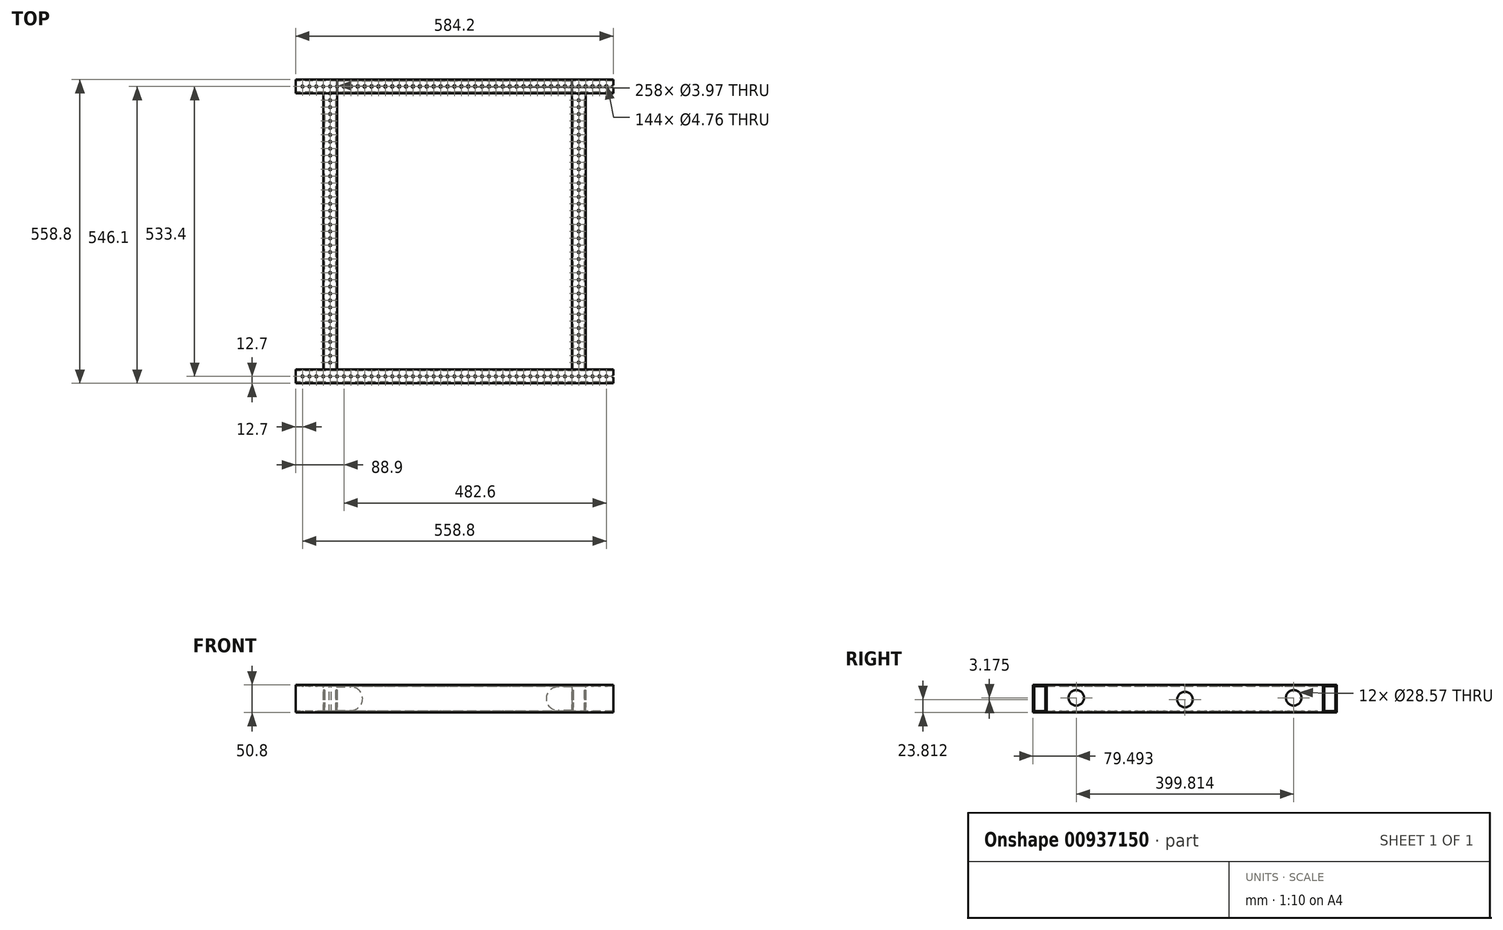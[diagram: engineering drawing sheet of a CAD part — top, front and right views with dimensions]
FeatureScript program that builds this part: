
annotation { "Feature Type Name" : "Feature", "Feature Type Description" : "" }
export const myFeature = defineFeature(function(context is Context, id is Id, definition is map)
    precondition{}
    {
        {
            var Q0;
            Q0=qCreatedBy(makeId("Right.planeOp"),FACE);
            var sketch = newSketch(context, id + "F0", { "sketchPlane" : qUnion([Q0])});
            skLineSegment(sketch, "E0.bottom", {"start": v(12.7, -25.4) * mm, "end": v(-12.7, -25.4) * mm});
            skLineSegment(sketch, "E0.top", {"start": v(12.7, 25.4) * mm, "end": v(-12.7, 25.4) * mm});
            skLineSegment(sketch, "E0.left", {"start": v(12.7, -25.4) * mm, "end": v(12.7, 25.4) * mm});
            skLineSegment(sketch, "E0.right", {"start": v(-12.7, -25.4) * mm, "end": v(-12.7, 25.4) * mm});
            skPoint(sketch, "E0.middle", {"position": v(0, 0) * mm});
            skLineSegment(sketch, "E1.0", {"start": v(10.16, 22.86) * mm, "end": v(-10.16, 22.86) * mm});
            skLineSegment(sketch, "E1.1", {"start": v(10.16, -22.86) * mm, "end": v(10.16, 22.86) * mm});
            skLineSegment(sketch, "E1.2", {"start": v(10.16, -22.86) * mm, "end": v(-10.16, -22.86) * mm});
            skLineSegment(sketch, "E1.3", {"start": v(-10.16, -22.86) * mm, "end": v(-10.16, 22.86) * mm});
            skSolve(sketch);
        }
        {
            var Q0;
            Q0 = qSketchRegion(id + "F0", true);
            extrude(context, id + "F1", {"entities" : qUnion([Q0]), "endBound" : BoundingType.SYMMETRIC, "depth" : 584.2 * mm, "offsetDistance" : 25.4 * mm});
        }
        {
            var Q0;
            Q0=makeQuery(id+"F1.opExtrude","SWEPT_FACE",FACE,{"disambiguationData":[OSD([sQuery(id+"F0.wireOp",EDGE,"E0.top")])]});
            var sketch = newSketch(context, id + "F2", { "sketchPlane" : qUnion([Q0])});
            skLineSegment(sketch, "E2", {"start": v(-292.1, 0) * mm, "end": v(292.1, 0) * mm, "construction": true});
            skCircle(sketch, "E3", {"center": v(-279.4, 0) * mm, "radius": 1.98 * mm});
            skCircle(sketch, "E4.1.0.0", {"center": v(-266.7, 0) * mm, "radius": 1.98 * mm});
            skCircle(sketch, "E4.2.0.0", {"center": v(-254, 0) * mm, "radius": 1.98 * mm});
            skCircle(sketch, "E4.3.0.0", {"center": v(-241.3, 0) * mm, "radius": 1.98 * mm});
            skCircle(sketch, "E4.4.0.0", {"center": v(-228.6, 0) * mm, "radius": 1.98 * mm});
            skCircle(sketch, "E4.5.0.0", {"center": v(-215.9, 0) * mm, "radius": 1.98 * mm});
            skCircle(sketch, "E4.6.0.0", {"center": v(-203.2, 0) * mm, "radius": 1.98 * mm});
            skCircle(sketch, "E4.7.0.0", {"center": v(-190.5, 0) * mm, "radius": 1.98 * mm});
            skCircle(sketch, "E4.8.0.0", {"center": v(-177.8, 0) * mm, "radius": 1.98 * mm});
            skCircle(sketch, "E4.9.0.0", {"center": v(-165.1, 0) * mm, "radius": 1.98 * mm});
            skCircle(sketch, "E4.10.0.0", {"center": v(-152.4, 0) * mm, "radius": 1.98 * mm});
            skCircle(sketch, "E4.11.0.0", {"center": v(-139.7, 0) * mm, "radius": 1.98 * mm});
            skCircle(sketch, "E4.12.0.0", {"center": v(-127, 0) * mm, "radius": 1.98 * mm});
            skCircle(sketch, "E4.13.0.0", {"center": v(-114.3, 0) * mm, "radius": 1.98 * mm});
            skCircle(sketch, "E4.14.0.0", {"center": v(-101.6, 0) * mm, "radius": 1.98 * mm});
            skCircle(sketch, "E4.15.0.0", {"center": v(-88.9, 0) * mm, "radius": 1.98 * mm});
            skCircle(sketch, "E4.16.0.0", {"center": v(-76.2, 0) * mm, "radius": 1.98 * mm});
            skCircle(sketch, "E4.17.0.0", {"center": v(-63.5, 0) * mm, "radius": 1.98 * mm});
            skCircle(sketch, "E4.18.0.0", {"center": v(-50.8, 0) * mm, "radius": 1.98 * mm});
            skCircle(sketch, "E4.19.0.0", {"center": v(-38.1, 0) * mm, "radius": 1.98 * mm});
            skCircle(sketch, "E4.20.0.0", {"center": v(-25.4, 0) * mm, "radius": 1.98 * mm});
            skCircle(sketch, "E4.21.0.0", {"center": v(-12.7, 0) * mm, "radius": 1.98 * mm});
            skCircle(sketch, "E4.22.0.0", {"center": v(0, 0) * mm, "radius": 1.98 * mm});
            skCircle(sketch, "E4.23.0.0", {"center": v(12.7, 0) * mm, "radius": 1.98 * mm});
            skCircle(sketch, "E4.24.0.0", {"center": v(25.4, 0) * mm, "radius": 1.98 * mm});
            skCircle(sketch, "E4.25.0.0", {"center": v(38.1, 0) * mm, "radius": 1.98 * mm});
            skCircle(sketch, "E4.26.0.0", {"center": v(50.8, 0) * mm, "radius": 1.98 * mm});
            skCircle(sketch, "E4.27.0.0", {"center": v(63.5, 0) * mm, "radius": 1.98 * mm});
            skCircle(sketch, "E4.28.0.0", {"center": v(76.2, 0) * mm, "radius": 1.98 * mm});
            skCircle(sketch, "E4.29.0.0", {"center": v(88.9, 0) * mm, "radius": 1.98 * mm});
            skCircle(sketch, "E4.30.0.0", {"center": v(101.6, 0) * mm, "radius": 1.98 * mm});
            skCircle(sketch, "E4.31.0.0", {"center": v(114.3, 0) * mm, "radius": 1.98 * mm});
            skCircle(sketch, "E4.32.0.0", {"center": v(127, 0) * mm, "radius": 1.98 * mm});
            skCircle(sketch, "E4.33.0.0", {"center": v(139.7, 0) * mm, "radius": 1.98 * mm});
            skCircle(sketch, "E4.34.0.0", {"center": v(152.4, 0) * mm, "radius": 1.98 * mm});
            skCircle(sketch, "E4.35.0.0", {"center": v(165.1, 0) * mm, "radius": 1.98 * mm});
            skCircle(sketch, "E4.36.0.0", {"center": v(177.8, 0) * mm, "radius": 1.98 * mm});
            skCircle(sketch, "E4.37.0.0", {"center": v(190.5, 0) * mm, "radius": 1.98 * mm});
            skCircle(sketch, "E4.38.0.0", {"center": v(203.2, 0) * mm, "radius": 1.98 * mm});
            skCircle(sketch, "E4.39.0.0", {"center": v(215.9, 0) * mm, "radius": 1.98 * mm});
            skCircle(sketch, "E4.40.0.0", {"center": v(228.6, 0) * mm, "radius": 1.98 * mm});
            skCircle(sketch, "E4.41.0.0", {"center": v(241.3, 0) * mm, "radius": 1.98 * mm});
            skCircle(sketch, "E4.42.0.0", {"center": v(254, 0) * mm, "radius": 1.98 * mm});
            skCircle(sketch, "E4.43.0.0", {"center": v(266.7, 0) * mm, "radius": 1.98 * mm});
            skCircle(sketch, "E4.44.0.0", {"center": v(279.4, 0) * mm, "radius": 1.98 * mm});
            skCircle(sketch, "E4.45.0.0", {"center": v(292.1, 0) * mm, "radius": 1.98 * mm});
            skCircle(sketch, "E4.46.0.0", {"center": v(304.8, 0) * mm, "radius": 1.98 * mm});
            skCircle(sketch, "E4.47.0.0", {"center": v(317.5, 0) * mm, "radius": 1.98 * mm});
            skCircle(sketch, "E4.48.0.0", {"center": v(330.2, 0) * mm, "radius": 1.98 * mm});
            skCircle(sketch, "E4.49.0.0", {"center": v(342.9, 0) * mm, "radius": 1.98 * mm});
            skCircle(sketch, "E4.50.0.0", {"center": v(355.6, 0) * mm, "radius": 1.98 * mm});
            skCircle(sketch, "E4.51.0.0", {"center": v(368.3, 0) * mm, "radius": 1.98 * mm});
            skCircle(sketch, "E4.52.0.0", {"center": v(381, 0) * mm, "radius": 1.98 * mm});
            skCircle(sketch, "E4.53.0.0", {"center": v(393.7, 0) * mm, "radius": 1.98 * mm});
            skCircle(sketch, "E4.54.0.0", {"center": v(406.4, 0) * mm, "radius": 1.98 * mm});
            skCircle(sketch, "E4.55.0.0", {"center": v(419.1, 0) * mm, "radius": 1.98 * mm});
            skCircle(sketch, "E4.56.0.0", {"center": v(431.8, 0) * mm, "radius": 1.98 * mm});
            skCircle(sketch, "E4.57.0.0", {"center": v(444.5, 0) * mm, "radius": 1.98 * mm});
            skCircle(sketch, "E4.58.0.0", {"center": v(457.2, 0) * mm, "radius": 1.98 * mm});
            skCircle(sketch, "E4.59.0.0", {"center": v(469.9, 0) * mm, "radius": 1.98 * mm});
            skLineSegment(sketch, "E4.direction1", {"start": v(-279.4, 0) * mm, "end": v(-266.7, 0) * mm, "construction": true});
            skSolve(sketch);
        }
        {
            var Q0;
            Q0 = qSketchRegion(id + "F2", true);
            extrude(context, id + "F3", {"entities" : qUnion([Q0]), "operationType" : NewBodyOperationType.REMOVE, "oppositeDirection" : true, "depth" : 76.2 * mm, "offsetDistance" : 25.4 * mm});
        }
        {
            var Q0;
            Q0=makeQuery(id+"F1.opExtrude","SWEPT_BODY",BODY,{"disambiguationData":[OSD([sQuery(id+"F0.wireOp",EDGE,"E0.bottom"),sQuery(id+"F0.wireOp",EDGE,"E0.top"),sQuery(id+"F0.wireOp",EDGE,"E0.left"),sQuery(id+"F0.wireOp",EDGE,"E0.right"),sQuery(id+"F0.wireOp",EDGE,"E1.0"),sQuery(id+"F0.wireOp",EDGE,"E1.1"),sQuery(id+"F0.wireOp",EDGE,"E1.2"),sQuery(id+"F0.wireOp",EDGE,"E1.3")])]});
            transform(context, id + "F4", {"entities" : qUnion([Q0]), "transformType" : TransformType.TRANSLATION_3D, "dx" : 0 * mm, "dy" : -533.4 * mm, "dz" : 0 * mm, "makeCopy" : true});
        }
        {
            var Q0;
            Q0=makeQuery(id+"F1.opExtrude","SWEPT_BODY",BODY,{"disambiguationData":[OSD([sQuery(id+"F0.wireOp",EDGE,"E0.bottom"),sQuery(id+"F0.wireOp",EDGE,"E0.top"),sQuery(id+"F0.wireOp",EDGE,"E0.left"),sQuery(id+"F0.wireOp",EDGE,"E0.right"),sQuery(id+"F0.wireOp",EDGE,"E1.0"),sQuery(id+"F0.wireOp",EDGE,"E1.1"),sQuery(id+"F0.wireOp",EDGE,"E1.2"),sQuery(id+"F0.wireOp",EDGE,"E1.3")])]});
            var Q1;
            Q1=makeQuery(id+"F1.opExtrude","CAP_EDGE",EDGE,{"disambiguationData":[OSD([sQuery(id+"F0.wireOp",EDGE,"E0.right")])],"isStart":true});
            transform(context, id + "F5", {"entities" : qUnion([Q0]), "transformType" : TransformType.ROTATION, "transformAxis" : qUnion([Q1]), "angle" : 270 * degree, "makeCopy" : true});
        }
        {
            var Q0;
            Q0=makeQuery(id+"F5.opPattern","COPY",BODY,{"derivedFrom":makeQuery(id+"F1.opExtrude","SWEPT_BODY",BODY,{"disambiguationData":[OSD([sQuery(id+"F0.wireOp",EDGE,"E0.bottom"),sQuery(id+"F0.wireOp",EDGE,"E0.top"),sQuery(id+"F0.wireOp",EDGE,"E0.left"),sQuery(id+"F0.wireOp",EDGE,"E0.right"),sQuery(id+"F0.wireOp",EDGE,"E1.0"),sQuery(id+"F0.wireOp",EDGE,"E1.1"),sQuery(id+"F0.wireOp",EDGE,"E1.2"),sQuery(id+"F0.wireOp",EDGE,"E1.3")])]}),"instanceName":"1"});
            deleteBodies(context, id + "F6", {"entities" : qUnion([Q0])});
        }
        {
            var Q0;
            Q0=makeQuery(id+"F1.opExtrude","SWEPT_FACE",FACE,{"disambiguationData":[OSD([sQuery(id+"F0.wireOp",EDGE,"E0.right")])]});
            var sketch = newSketch(context, id + "F7", { "sketchPlane" : qUnion([Q0])});
            skLineSegment(sketch, "E5.bottom", {"start": v(-215.9, -25.4) * mm, "end": v(-241.3, -25.4) * mm});
            skLineSegment(sketch, "E5.top", {"start": v(-215.9, 25.4) * mm, "end": v(-241.3, 25.4) * mm});
            skLineSegment(sketch, "E5.left", {"start": v(-215.9, -25.4) * mm, "end": v(-215.9, 25.4) * mm});
            skLineSegment(sketch, "E5.right", {"start": v(-241.3, -25.4) * mm, "end": v(-241.3, 25.4) * mm});
            skPoint(sketch, "E5.middle", {"position": v(-228.6, 0) * mm});
            skLineSegment(sketch, "E6.0", {"start": v(-218.44, 22.86) * mm, "end": v(-238.76, 22.86) * mm});
            skLineSegment(sketch, "E6.1", {"start": v(-218.44, -22.86) * mm, "end": v(-218.44, 22.86) * mm});
            skLineSegment(sketch, "E6.2", {"start": v(-218.44, -22.86) * mm, "end": v(-238.76, -22.86) * mm});
            skLineSegment(sketch, "E6.3", {"start": v(-238.76, -22.86) * mm, "end": v(-238.76, 22.86) * mm});
            skSolve(sketch);
        }
        {
            var Q0;
            Q0 = qSketchRegion(id + "F7", true);
            extrude(context, id + "F8", {"entities" : qUnion([Q0]), "depth" : 508 * mm, "offsetDistance" : 25.4 * mm});
        }
        {
            var Q0;
            Q0=makeQuery(id+"F8.opExtrude","SWEPT_FACE",FACE,{"disambiguationData":[OSD([sQuery(id+"F7.wireOp",EDGE,"E5.top")])]});
            var sketch = newSketch(context, id + "F9", { "sketchPlane" : qUnion([Q0])});
            skLineSegment(sketch, "E7", {"start": v(-228.6, -12.7) * mm, "end": v(-228.6, -520.7) * mm, "construction": true});
            skCircle(sketch, "E8", {"center": v(-228.6, -12.7) * mm, "radius": 1.98 * mm});
            skCircle(sketch, "E9.0.1.0", {"center": v(-228.6, -25.4) * mm, "radius": 1.98 * mm});
            skCircle(sketch, "E9.0.2.0", {"center": v(-228.6, -38.1) * mm, "radius": 1.98 * mm});
            skCircle(sketch, "E9.0.3.0", {"center": v(-228.6, -50.8) * mm, "radius": 1.98 * mm});
            skCircle(sketch, "E9.0.4.0", {"center": v(-228.6, -63.5) * mm, "radius": 1.98 * mm});
            skCircle(sketch, "E9.0.5.0", {"center": v(-228.6, -76.2) * mm, "radius": 1.98 * mm});
            skCircle(sketch, "E9.0.6.0", {"center": v(-228.6, -88.9) * mm, "radius": 1.98 * mm});
            skCircle(sketch, "E9.0.7.0", {"center": v(-228.6, -101.6) * mm, "radius": 1.98 * mm});
            skCircle(sketch, "E9.0.8.0", {"center": v(-228.6, -114.3) * mm, "radius": 1.98 * mm});
            skCircle(sketch, "E9.0.9.0", {"center": v(-228.6, -127) * mm, "radius": 1.98 * mm});
            skCircle(sketch, "E9.0.10.0", {"center": v(-228.6, -139.7) * mm, "radius": 1.98 * mm});
            skCircle(sketch, "E9.0.11.0", {"center": v(-228.6, -152.4) * mm, "radius": 1.98 * mm});
            skCircle(sketch, "E9.0.12.0", {"center": v(-228.6, -165.1) * mm, "radius": 1.98 * mm});
            skCircle(sketch, "E9.0.13.0", {"center": v(-228.6, -177.8) * mm, "radius": 1.98 * mm});
            skCircle(sketch, "E9.0.14.0", {"center": v(-228.6, -190.5) * mm, "radius": 1.98 * mm});
            skCircle(sketch, "E9.0.15.0", {"center": v(-228.6, -203.2) * mm, "radius": 1.98 * mm});
            skCircle(sketch, "E9.0.16.0", {"center": v(-228.6, -215.9) * mm, "radius": 1.98 * mm});
            skCircle(sketch, "E9.0.17.0", {"center": v(-228.6, -228.6) * mm, "radius": 1.98 * mm});
            skCircle(sketch, "E9.0.18.0", {"center": v(-228.6, -241.3) * mm, "radius": 1.98 * mm});
            skCircle(sketch, "E9.0.19.0", {"center": v(-228.6, -254) * mm, "radius": 1.98 * mm});
            skCircle(sketch, "E9.0.20.0", {"center": v(-228.6, -266.7) * mm, "radius": 1.98 * mm});
            skCircle(sketch, "E9.0.21.0", {"center": v(-228.6, -279.4) * mm, "radius": 1.98 * mm});
            skCircle(sketch, "E9.0.22.0", {"center": v(-228.6, -292.1) * mm, "radius": 1.98 * mm});
            skCircle(sketch, "E9.0.23.0", {"center": v(-228.6, -304.8) * mm, "radius": 1.98 * mm});
            skCircle(sketch, "E9.0.24.0", {"center": v(-228.6, -317.5) * mm, "radius": 1.98 * mm});
            skCircle(sketch, "E9.0.25.0", {"center": v(-228.6, -330.2) * mm, "radius": 1.98 * mm});
            skCircle(sketch, "E9.0.26.0", {"center": v(-228.6, -342.9) * mm, "radius": 1.98 * mm});
            skCircle(sketch, "E9.0.27.0", {"center": v(-228.6, -355.6) * mm, "radius": 1.98 * mm});
            skCircle(sketch, "E9.0.28.0", {"center": v(-228.6, -368.3) * mm, "radius": 1.98 * mm});
            skCircle(sketch, "E9.0.29.0", {"center": v(-228.6, -381) * mm, "radius": 1.98 * mm});
            skCircle(sketch, "E9.0.30.0", {"center": v(-228.6, -393.7) * mm, "radius": 1.98 * mm});
            skCircle(sketch, "E9.0.31.0", {"center": v(-228.6, -406.4) * mm, "radius": 1.98 * mm});
            skLineSegment(sketch, "E9.direction1", {"start": v(-228.6, -12.7) * mm, "end": v(-190.5, -12.7) * mm, "construction": true});
            skLineSegment(sketch, "E9.direction2", {"start": v(-228.6, -12.7) * mm, "end": v(-228.6, -25.4) * mm, "construction": true});
            skCircle(sketch, "E10.0.0.32", {"center": v(-228.6, -419.1) * mm, "radius": 1.98 * mm});
            skCircle(sketch, "E10.0.0.33", {"center": v(-228.6, -431.8) * mm, "radius": 1.98 * mm});
            skCircle(sketch, "E10.0.0.34", {"center": v(-228.6, -444.5) * mm, "radius": 1.98 * mm});
            skCircle(sketch, "E10.0.0.35", {"center": v(-228.6, -457.2) * mm, "radius": 1.98 * mm});
            skCircle(sketch, "E10.0.0.36", {"center": v(-228.6, -469.9) * mm, "radius": 1.98 * mm});
            skCircle(sketch, "E10.0.0.37", {"center": v(-228.6, -482.6) * mm, "radius": 1.98 * mm});
            skCircle(sketch, "E10.0.0.38", {"center": v(-228.6, -495.3) * mm, "radius": 1.98 * mm});
            skCircle(sketch, "E10.0.0.39", {"center": v(-228.6, -508) * mm, "radius": 1.98 * mm});
            skSolve(sketch);
        }
        {
            var Q0;
            Q0 = qSketchRegion(id + "F9", true);
            extrude(context, id + "F10", {"entities" : qUnion([Q0]), "operationType" : NewBodyOperationType.REMOVE, "oppositeDirection" : true, "depth" : 76.2 * mm, "offsetDistance" : 25.4 * mm});
        }
        {
            var Q0;
            Q0=makeQuery(id+"F8.opExtrude","SWEPT_FACE",FACE,{"disambiguationData":[OSD([sQuery(id+"F7.wireOp",EDGE,"E5.right")])]});
            var sketch = newSketch(context, id + "F11", { "sketchPlane" : qUnion([Q0])});
            skLineSegment(sketch, "E11", {"start": v(12.7, 0) * mm, "end": v(520.7, 0) * mm, "construction": true});
            skLineSegment(sketch, "E12", {"start": v(266.7, -25.4) * mm, "end": v(266.7, 25.4) * mm, "construction": true});
            skCircle(sketch, "E13", {"center": v(266.7, -1.59) * mm, "radius": 14.29 * mm});
            skCircle(sketch, "E14", {"center": v(466.6, 1.59) * mm, "radius": 14.29 * mm});
            skCircle(sketch, "E15.MirrorC", {"center": v(66.8, 1.59) * mm, "radius": 14.29 * mm});
            skSolve(sketch);
        }
        {
            var Q0;
            Q0 = qSketchRegion(id + "F11", true);
            extrude(context, id + "F12", {"entities" : qUnion([Q0]), "operationType" : NewBodyOperationType.REMOVE, "endBound" : BoundingType.SYMMETRIC, "oppositeDirection" : true, "depth" : 1524 * mm, "offsetDistance" : 25.4 * mm});
        }
        {
            var Q0;
            Q0=makeQuery(id+"F8.opExtrude","SWEPT_BODY",BODY,{"disambiguationData":[OSD([sQuery(id+"F7.wireOp",EDGE,"E5.bottom"),sQuery(id+"F7.wireOp",EDGE,"E5.top"),sQuery(id+"F7.wireOp",EDGE,"E5.left"),sQuery(id+"F7.wireOp",EDGE,"E5.right"),sQuery(id+"F7.wireOp",EDGE,"E6.0"),sQuery(id+"F7.wireOp",EDGE,"E6.1"),sQuery(id+"F7.wireOp",EDGE,"E6.2"),sQuery(id+"F7.wireOp",EDGE,"E6.3")])]});
            var Q1;
            Q1=qCreatedBy(makeId("Right.planeOp"),FACE);
            mirror(context, id + "F13", {"entities" : qUnion([Q0]), "mirrorPlane" : qUnion([Q1])});
        }
        {
            var Q0;
            Q0=qCreatedBy(makeId("Right.planeOp"),FACE);
            var sketch = newSketch(context, id + "F14", { "sketchPlane" : qUnion([Q0])});
            skLineSegment(sketch, "E16.0", {"start": v(12.7, -25.4) * mm, "end": v(-12.7, -25.4) * mm});
            skLineSegment(sketch, "E16.1", {"start": v(-12.7, -25.4) * mm, "end": v(-12.7, 25.4) * mm});
            skLineSegment(sketch, "E16.2", {"start": v(10.16, 22.86) * mm, "end": v(-10.16, 22.86) * mm});
            skLineSegment(sketch, "E16.3", {"start": v(10.16, -22.86) * mm, "end": v(10.16, 22.86) * mm});
            skLineSegment(sketch, "E16.4", {"start": v(10.16, -22.86) * mm, "end": v(-10.16, -22.86) * mm});
            skLineSegment(sketch, "E16.5", {"start": v(-10.16, -22.86) * mm, "end": v(-10.16, 22.86) * mm});
            skLineSegment(sketch, "E17.0", {"start": v(12.7, 25.4) * mm, "end": v(-12.7, 25.4) * mm});
            skLineSegment(sketch, "E17.1", {"start": v(12.7, -25.4) * mm, "end": v(12.7, 25.4) * mm});
            skSolve(sketch);
        }
        {
            var Q0;
            Q0 = qSketchRegion(id + "F14", true);
            var Q1;
            Q1=makeQuery(id+"F8.opExtrude","SWEPT_FACE",FACE,{"disambiguationData":[OSD([sQuery(id+"F7.wireOp",EDGE,"E5.left")])]});
            var Q2;
            Q2=makeQuery(id+"F13.opPattern","COPY",FACE,{"derivedFrom":makeQuery(id+"F8.opExtrude","SWEPT_FACE",FACE,{"disambiguationData":[OSD([sQuery(id+"F7.wireOp",EDGE,"E5.left")])]}),"instanceName":"1"});
            extrude(context, id + "F15", {"entities" : qUnion([Q0]), "endBound" : BoundingType.UP_TO_SURFACE, "oppositeDirection" : true, "depth" : 25.4 * mm, "endBoundEntityFace" : qUnion([Q1]), "offsetDistance" : 25.4 * mm, "hasSecondDirection" : true, "secondDirectionBound" : SecondDirectionBoundingType.UP_TO_SURFACE, "secondDirectionOppositeDirection" : false, "secondDirectionDepth" : 25.4 * mm, "secondDirectionBoundEntityFace" : qUnion([Q2])});
        }
        {
            var Q0;
            Q0=makeQuery(id+"F15.opExtrude","SWEPT_FACE",FACE,{"disambiguationData":[OSD([sQuery(id+"F14.wireOp",EDGE,"E17.0")])]});
            var sketch = newSketch(context, id + "F16", { "sketchPlane" : qUnion([Q0])});
            skCircle(sketch, "E18", {"center": v(-203.2, 0) * mm, "radius": 2.38 * mm});
            skPoint(sketch, "E18.centerSnap0", {"position": v(-215.9, 0) * mm});
            skCircle(sketch, "E19.1.0.0", {"center": v(-190.5, 0) * mm, "radius": 2.38 * mm});
            skCircle(sketch, "E19.2.0.0", {"center": v(-177.8, 0) * mm, "radius": 2.38 * mm});
            skCircle(sketch, "E19.3.0.0", {"center": v(-165.1, 0) * mm, "radius": 2.38 * mm});
            skCircle(sketch, "E19.4.0.0", {"center": v(-152.4, 0) * mm, "radius": 2.38 * mm});
            skCircle(sketch, "E19.5.0.0", {"center": v(-139.7, 0) * mm, "radius": 2.38 * mm});
            skCircle(sketch, "E19.6.0.0", {"center": v(-127, 0) * mm, "radius": 2.38 * mm});
            skCircle(sketch, "E19.7.0.0", {"center": v(-114.3, 0) * mm, "radius": 2.38 * mm});
            skCircle(sketch, "E19.8.0.0", {"center": v(-101.6, 0) * mm, "radius": 2.38 * mm});
            skCircle(sketch, "E19.9.0.0", {"center": v(-88.9, 0) * mm, "radius": 2.38 * mm});
            skCircle(sketch, "E19.10.0.0", {"center": v(-76.2, 0) * mm, "radius": 2.38 * mm});
            skCircle(sketch, "E19.11.0.0", {"center": v(-63.5, 0) * mm, "radius": 2.38 * mm});
            skCircle(sketch, "E19.12.0.0", {"center": v(-50.8, 0) * mm, "radius": 2.38 * mm});
            skCircle(sketch, "E19.13.0.0", {"center": v(-38.1, 0) * mm, "radius": 2.38 * mm});
            skCircle(sketch, "E19.14.0.0", {"center": v(-25.4, 0) * mm, "radius": 2.38 * mm});
            skCircle(sketch, "E19.15.0.0", {"center": v(-12.7, 0) * mm, "radius": 2.38 * mm});
            skCircle(sketch, "E19.16.0.0", {"center": v(0, 0) * mm, "radius": 2.38 * mm});
            skCircle(sketch, "E19.17.0.0", {"center": v(12.7, 0) * mm, "radius": 2.38 * mm});
            skCircle(sketch, "E19.18.0.0", {"center": v(25.4, 0) * mm, "radius": 2.38 * mm});
            skCircle(sketch, "E19.19.0.0", {"center": v(38.1, 0) * mm, "radius": 2.38 * mm});
            skCircle(sketch, "E19.20.0.0", {"center": v(50.8, 0) * mm, "radius": 2.38 * mm});
            skCircle(sketch, "E19.21.0.0", {"center": v(63.5, 0) * mm, "radius": 2.38 * mm});
            skCircle(sketch, "E19.22.0.0", {"center": v(76.2, 0) * mm, "radius": 2.38 * mm});
            skCircle(sketch, "E19.23.0.0", {"center": v(88.9, 0) * mm, "radius": 2.38 * mm});
            skCircle(sketch, "E19.24.0.0", {"center": v(101.6, 0) * mm, "radius": 2.38 * mm});
            skCircle(sketch, "E19.25.0.0", {"center": v(114.3, 0) * mm, "radius": 2.38 * mm});
            skCircle(sketch, "E19.26.0.0", {"center": v(127, 0) * mm, "radius": 2.38 * mm});
            skCircle(sketch, "E19.27.0.0", {"center": v(139.7, 0) * mm, "radius": 2.38 * mm});
            skCircle(sketch, "E19.28.0.0", {"center": v(152.4, 0) * mm, "radius": 2.38 * mm});
            skCircle(sketch, "E19.29.0.0", {"center": v(165.1, 0) * mm, "radius": 2.38 * mm});
            skCircle(sketch, "E19.30.0.0", {"center": v(177.8, 0) * mm, "radius": 2.38 * mm});
            skCircle(sketch, "E19.31.0.0", {"center": v(190.5, 0) * mm, "radius": 2.38 * mm});
            skCircle(sketch, "E19.32.0.0", {"center": v(203.2, 0) * mm, "radius": 2.38 * mm});
            skCircle(sketch, "E19.33.0.0", {"center": v(215.9, 0) * mm, "radius": 2.38 * mm});
            skCircle(sketch, "E19.34.0.0", {"center": v(228.6, 0) * mm, "radius": 2.38 * mm});
            skCircle(sketch, "E19.35.0.0", {"center": v(241.3, 0) * mm, "radius": 2.38 * mm});
            skCircle(sketch, "E19.36.0.0", {"center": v(254, 0) * mm, "radius": 2.38 * mm});
            skCircle(sketch, "E19.37.0.0", {"center": v(266.7, 0) * mm, "radius": 2.38 * mm});
            skCircle(sketch, "E19.38.0.0", {"center": v(279.4, 0) * mm, "radius": 2.38 * mm});
            skCircle(sketch, "E19.39.0.0", {"center": v(292.1, 0) * mm, "radius": 2.38 * mm});
            skLineSegment(sketch, "E19.direction1", {"start": v(-203.2, 0) * mm, "end": v(-190.5, 0) * mm, "construction": true});
            skSolve(sketch);
        }
        {
            var Q0;
            Q0 = qSketchRegion(id + "F16", true);
            extrude(context, id + "F17", {"entities" : qUnion([Q0]), "operationType" : NewBodyOperationType.REMOVE, "endBound" : BoundingType.THROUGH_ALL, "oppositeDirection" : true, "depth" : 25.4 * mm, "offsetDistance" : 25.4 * mm});
        }
        {
            var Q0;
            {var subQ0=sQuery(id+"F7.wireOp",EDGE,"E5.left");Q0=makeQuery(id+"F7.imprint","IMPRINT",FACE,{"disambiguationData":[TD([[makeQuery(id+"F7.imprint","IMPRINT",EDGE,{"derivedFrom":subQ0}),-1.0]])]});}
            var sketch = newSketch(context, id + "F18", { "sketchPlane" : qUnion([Q0])});
            skArc(sketch, "E20", {"start": v(-204.46, 16.47) * mm, "mid": v(-168.98, -1.76) * mm, "end": v(-206.95, -13.98) * mm});
            skLineSegment(sketch, "E21.bottom", {"start": v(-190.5, -21.59) * mm, "end": v(-215.9, -21.59) * mm});
            skLineSegment(sketch, "E21.top", {"start": v(-190.5, 21.59) * mm, "end": v(-215.9, 21.59) * mm});
            skLineSegment(sketch, "E21.left", {"start": v(-190.5, -21.59) * mm, "end": v(-190.5, 21.59) * mm});
            skLineSegment(sketch, "E21.right", {"start": v(-215.9, -21.59) * mm, "end": v(-215.9, 21.6) * mm});
            skPoint(sketch, "E21.middle", {"position": v(-203.2, 0) * mm});
            skLineSegment(sketch, "E22.MirrorCS", {"start": v(190.5, 21.59) * mm, "end": v(215.9, 21.59) * mm});
            skArc(sketch, "E23.MirrorCS", {"start": v(204.46, 16.47) * mm, "mid": v(168.98, -1.76) * mm, "end": v(206.95, -13.98) * mm});
            skLineSegment(sketch, "E24.MirrorCS", {"start": v(190.5, -21.59) * mm, "end": v(215.9, -21.59) * mm});
            skLineSegment(sketch, "E25.MirrorCS", {"start": v(190.5, -21.59) * mm, "end": v(190.5, 21.59) * mm});
            skLineSegment(sketch, "E26", {"start": v(215.9, 21.59) * mm, "end": v(215.9, -21.59) * mm});
            skSolve(sketch);
        }
        {
            var Q0;
            Q0 = qSketchRegion(id + "F18", true);
            extrude(context, id + "F19", {"entities" : qUnion([Q0]), "operationType" : NewBodyOperationType.REMOVE, "oppositeDirection" : true, "depth" : 27.94 * mm, "offsetDistance" : 25.4 * mm});
        }
    });
